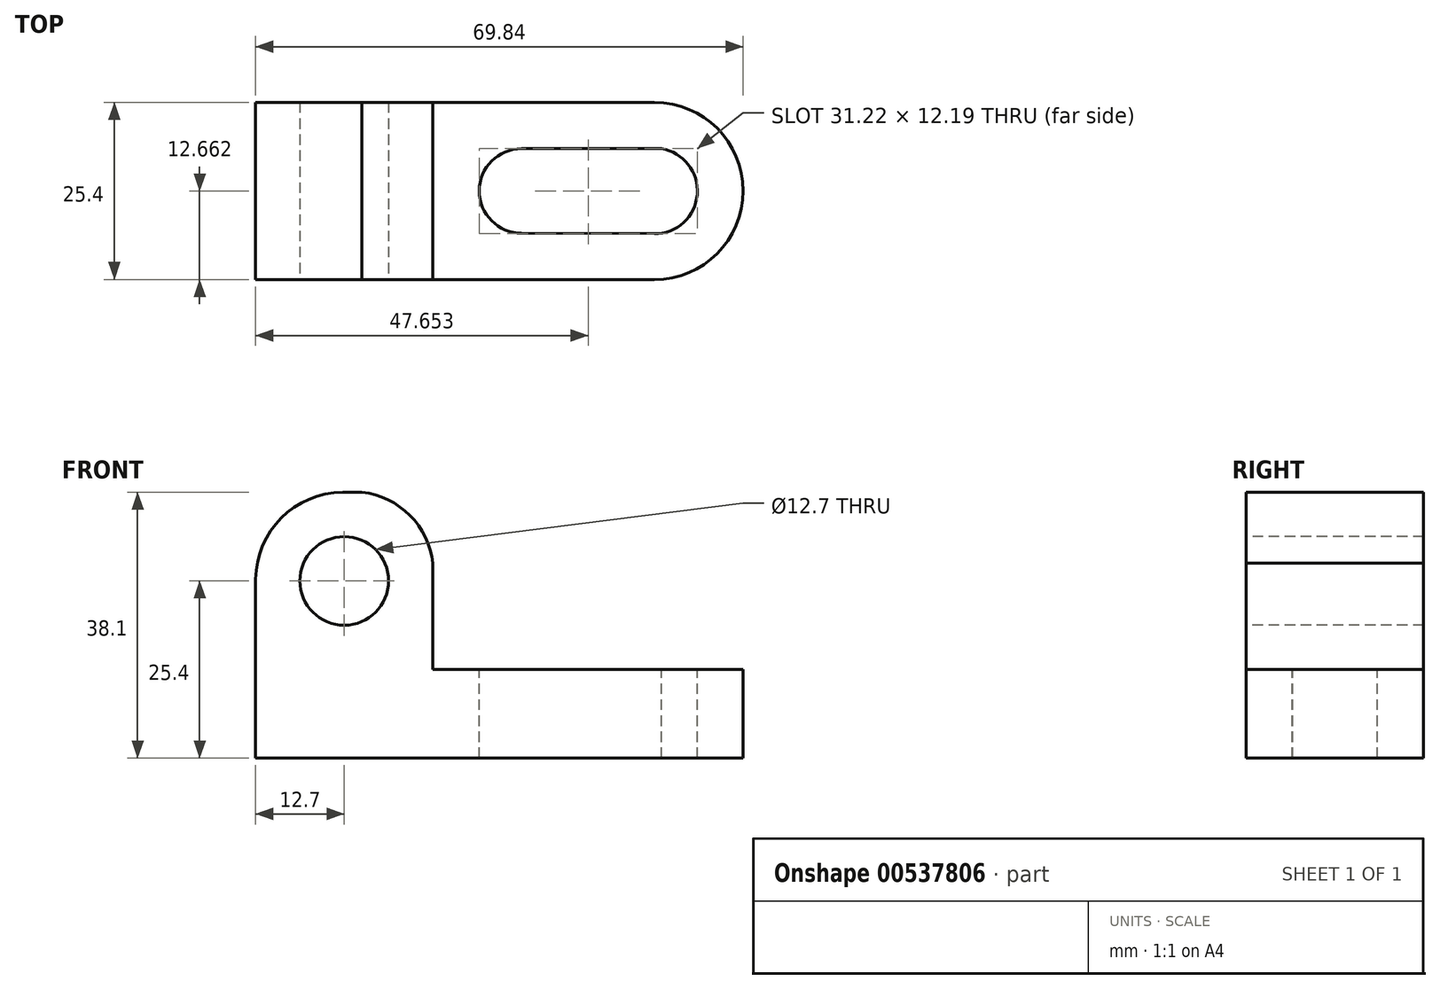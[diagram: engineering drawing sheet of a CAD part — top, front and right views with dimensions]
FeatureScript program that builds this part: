
annotation { "Feature Type Name" : "Feature", "Feature Type Description" : "" }
export const myFeature = defineFeature(function(context is Context, id is Id, definition is map)
    precondition{}
    {
        {
            var Q0;
            Q0=qCreatedBy(makeId("Front.planeOp"),FACE);
            var sketch = newSketch(context, id + "F0", { "sketchPlane" : qUnion([Q0])});
            skLineSegment(sketch, "E0", {"start": v(0, 0) * mm, "end": v(69.85, 0) * mm});
            skLineSegment(sketch, "E1", {"start": v(69.85, 0) * mm, "end": v(69.85, 12.7) * mm});
            skLineSegment(sketch, "E2", {"start": v(69.85, 12.7) * mm, "end": v(25.4, 12.7) * mm});
            skLineSegment(sketch, "E3", {"start": v(25.4, 12.7) * mm, "end": v(25.4, 38.1) * mm});
            skLineSegment(sketch, "E4", {"start": v(25.4, 38.1) * mm, "end": v(0, 38.1) * mm});
            skLineSegment(sketch, "E5", {"start": v(0, 38.1) * mm, "end": v(0, 0) * mm});
            skSolve(sketch);
        }
        {
            var Q0;
            Q0=makeQuery(id+"F0.imprint","IMPRINT",FACE,{"disambiguationData":[TD([[makeQuery(id+"F0.imprint","IMPRINT",EDGE,{"derivedFrom":sQuery(id+"F0.wireOp",EDGE,"E0")}),1.0]])]});
            extrude(context, id + "F1", {"entities" : qUnion([Q0]), "depth" : 25.4 * mm, "offsetDistance" : 25.4 * mm});
        }
        {
            var Q0;
            Q0=makeQuery(id+"F1.opExtrude","CAP_FACE",FACE,{"disambiguationData":[OSD([sQuery(id+"F0.wireOp",EDGE,"E0"),sQuery(id+"F0.wireOp",EDGE,"E1"),sQuery(id+"F0.wireOp",EDGE,"E2"),sQuery(id+"F0.wireOp",EDGE,"E3"),sQuery(id+"F0.wireOp",EDGE,"E4"),sQuery(id+"F0.wireOp",EDGE,"E5")])],"isStart":false});
            var sketch = newSketch(context, id + "F2", { "sketchPlane" : qUnion([Q0])});
            skCircle(sketch, "E6", {"center": v(12.7, 25.4) * mm, "radius": 6.35 * mm});
            skArc(sketch, "E7", {"start": v(25.4, 25.4) * mm, "mid": v(22.1, 34.8) * mm, "end": v(12.7, 38.1) * mm});
            skPoint(sketch, "E8.end.orphan", {"position": v(0, 25.4) * mm});
            skArc(sketch, "E9", {"start": v(12.7, 38.1) * mm, "mid": v(3.69, 34.41) * mm, "end": v(0, 25.4) * mm});
            skSolve(sketch);
        }
        {
            var Q0;
            Q0=makeQuery(id+"F2.imprint","IMPRINT",FACE,{"disambiguationData":[TD([[makeQuery(id+"F2.imprint","IMPRINT",EDGE,{"derivedFrom":sQuery(id+"F2.wireOp",EDGE,"E6")}),1.0]])]});
            var Q1;
            {var subQ0=sQuery(id+"F2.wireOp",EDGE,"E8");var subQ1=makeQuery(id+"F1.opExtrude","CAP_EDGE",EDGE,{"disambiguationData":[OSD([sQuery(id+"F0.wireOp",EDGE,"E4")])],"isStart":false});var subQ2=makeQuery(id+"F2.imprint","INTERSECT",VERTEX,{"derivedFrom":[subQ1,subQ0]});Q1=makeQuery(id+"F2.imprint","IMPRINT",FACE,{"disambiguationData":[TD([[makeQuery(id+"F2.imprint","IMPRINT",EDGE,{"disambiguationData":[TD([[subQ2,-1.0]])],"derivedFrom":subQ0}),-1.0]])]});}
            var Q2;
            {var subQ0=sQuery(id+"F2.wireOp",EDGE,"E7");var subQ1=makeQuery(id+"F1.opExtrude","CAP_EDGE",EDGE,{"disambiguationData":[OSD([sQuery(id+"F0.wireOp",EDGE,"E3")])],"isStart":false});var subQ2=makeQuery(id+"F2.imprint","INTERSECT",VERTEX,{"disambiguationData":[OD(1.0)],"derivedFrom":[subQ1,subQ0]});Q2=makeQuery(id+"F2.imprint","IMPRINT",FACE,{"disambiguationData":[TD([[makeQuery(id+"F2.imprint","IMPRINT",EDGE,{"disambiguationData":[TD([[subQ2,-1.0]])],"derivedFrom":subQ0}),-1.0]])]});}
            var Q3;
            {var subQ0=sQuery(id+"F2.wireOp",EDGE,"E9");var subQ1=makeQuery(id+"F1.opExtrude","CAP_EDGE",EDGE,{"disambiguationData":[OSD([sQuery(id+"F0.wireOp",EDGE,"E4")])],"isStart":false});var subQ2=makeQuery(id+"F2.imprint","INTERSECT",VERTEX,{"derivedFrom":[subQ1,subQ0]});Q3=makeQuery(id+"F2.imprint","IMPRINT",FACE,{"disambiguationData":[TD([[makeQuery(id+"F2.imprint","IMPRINT",EDGE,{"disambiguationData":[TD([[subQ2,-1.0]])],"derivedFrom":subQ0}),-1.0]])]});}
            extrude(context, id + "F3", {"entities" : qUnion([Q0, Q1, Q2, Q3]), "operationType" : NewBodyOperationType.REMOVE, "oppositeDirection" : true, "depth" : 25.4 * mm, "offsetDistance" : 25.4 * mm});
        }
        {
            var Q0;
            Q0=makeQuery(id+"F1.opExtrude","SWEPT_FACE",FACE,{"disambiguationData":[OSD([sQuery(id+"F0.wireOp",EDGE,"E2")])]});
            var sketch = newSketch(context, id + "F4", { "sketchPlane" : qUnion([Q0])});
            skArc(sketch, "E10", {"start": v(38.1, -6.64) * mm, "mid": v(32.04, -12.7) * mm, "end": v(38.1, -18.76) * mm});
            skArc(sketch, "E11", {"start": v(57.13, -18.83) * mm, "mid": v(63.26, -12.23) * mm, "end": v(56.19, -6.64) * mm});
            skLineSegment(sketch, "E12", {"start": v(38.1, -18.76) * mm, "end": v(57.13, -18.83) * mm});
            skLineSegment(sketch, "E13", {"start": v(38.1, -6.64) * mm, "end": v(58.11, -6.64) * mm});
            skArc(sketch, "E14", {"start": v(57.15, -25.4) * mm, "mid": v(69.85, -12.7) * mm, "end": v(57.15, 0) * mm});
            skSolve(sketch);
        }
        {
            var Q0;
            {var subQ1=sQuery(id+"F4.wireOp",EDGE,"E10");Q0=makeQuery(id+"F4.imprint","IMPRINT",FACE,{"disambiguationData":[TD([[makeQuery(id+"F4.imprint","IMPRINT",EDGE,{"derivedFrom":subQ1}),1.0]])]});}
            extrude(context, id + "F5", {"entities" : qUnion([Q0]), "operationType" : NewBodyOperationType.REMOVE, "oppositeDirection" : true, "depth" : 12.7 * mm, "offsetDistance" : 25.4 * mm});
        }
        {
            var Q0;
            Q0=makeQuery(id+"F1.opExtrude","SWEPT_FACE",FACE,{"disambiguationData":[OSD([sQuery(id+"F0.wireOp",EDGE,"E2")])]});
            var sketch = newSketch(context, id + "F6", { "sketchPlane" : qUnion([Q0])});
            skArc(sketch, "E15", {"start": v(57.13, -25.4) * mm, "mid": v(69.84, -12.71) * mm, "end": v(57.15, 0) * mm});
            skSolve(sketch);
        }
        {
            var Q0;
            {var subQ0=sQuery(id+"F6.wireOp",EDGE,"E15");var subQ1=sQuery(id+"F0.wireOp",EDGE,"E2");var subQ2=makeQuery(id+"F1.opExtrude","CAP_EDGE",EDGE,{"disambiguationData":[OSD([subQ1])],"isStart":true});var subQ3=makeQuery(id+"F6.imprint","INTERSECT",VERTEX,{"derivedFrom":[subQ2,subQ0]});Q0=makeQuery(id+"F6.imprint","IMPRINT",FACE,{"disambiguationData":[TD([[makeQuery(id+"F6.imprint","IMPRINT",EDGE,{"disambiguationData":[TD([[subQ3,1.0]])],"derivedFrom":subQ0}),-1.0]])]});}
            var Q1;
            {var subQ0=sQuery(id+"F6.wireOp",EDGE,"E15");var subQ1=sQuery(id+"F0.wireOp",EDGE,"E2");var subQ4=makeQuery(id+"F1.opExtrude","SWEPT_EDGE",EDGE,{"disambiguationData":[OSD([sQuery(id+"F0.wireOp",EDGE,"E1"),subQ1])]});var subQ5=makeQuery(id+"F6.imprint","INTERSECT",VERTEX,{"disambiguationData":[OD(0.0)],"derivedFrom":[subQ4,subQ0]});Q1=makeQuery(id+"F6.imprint","IMPRINT",FACE,{"disambiguationData":[TD([[makeQuery(id+"F6.imprint","IMPRINT",EDGE,{"disambiguationData":[TD([[subQ5,1.0]])],"derivedFrom":subQ0}),-1.0]])]});}
            extrude(context, id + "F7", {"entities" : qUnion([Q0, Q1]), "operationType" : NewBodyOperationType.REMOVE, "oppositeDirection" : true, "depth" : 25.4 * mm, "offsetDistance" : 25.4 * mm});
        }
    });
